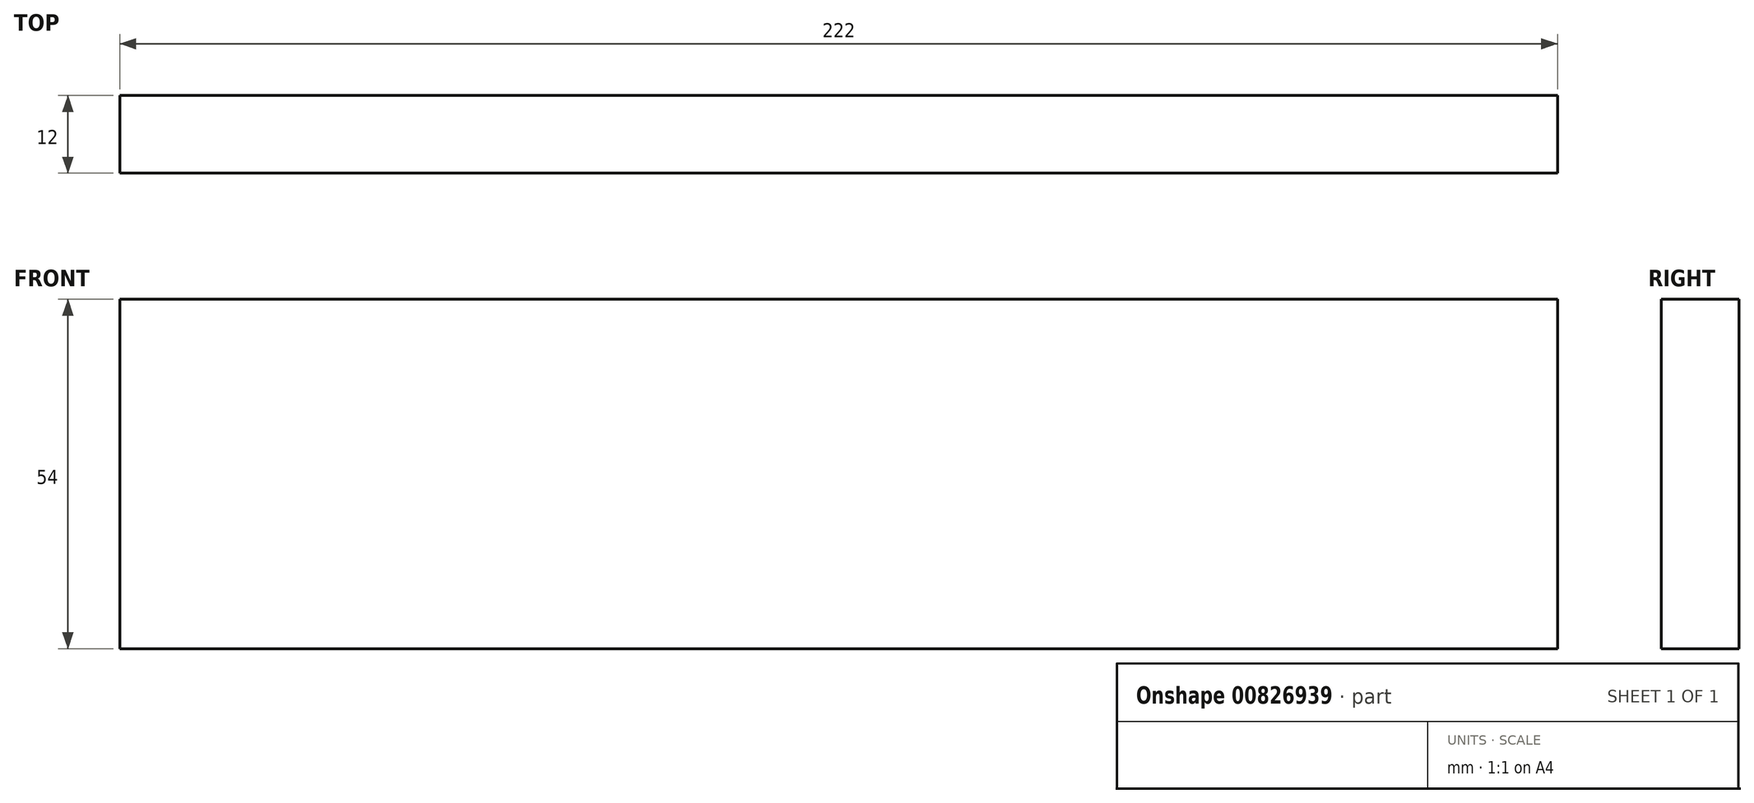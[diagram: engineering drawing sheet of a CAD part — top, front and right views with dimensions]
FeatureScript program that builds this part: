
annotation { "Feature Type Name" : "Feature", "Feature Type Description" : "" }
export const myFeature = defineFeature(function(context is Context, id is Id, definition is map)
    precondition{}
    {
        {
            var Q0;
            Q0=qCreatedBy(makeId("Front.planeOp"),FACE);
            var sketch = newSketch(context, id + "F0", { "sketchPlane" : qUnion([Q0])});
            skLineSegment(sketch, "E0.bottom", {"start": v(-111, 30.77) * mm, "end": v(111, 30.77) * mm});
            skLineSegment(sketch, "E0.top", {"start": v(-111, -23.23) * mm, "end": v(111, -23.23) * mm});
            skLineSegment(sketch, "E0.left", {"start": v(-111, 30.77) * mm, "end": v(-111, -23.23) * mm});
            skLineSegment(sketch, "E0.right", {"start": v(111, 30.77) * mm, "end": v(111, -23.23) * mm});
            skPoint(sketch, "E0.middle", {"position": v(0, 3.77) * mm});
            skSolve(sketch);
        }
        {
            var Q0;
            Q0 = qSketchRegion(id + "F0", true);
            extrude(context, id + "F1", {"entities" : qUnion([Q0]), "depth" : 12 * mm, "offsetDistance" : 25.4 * mm});
        }
    });
